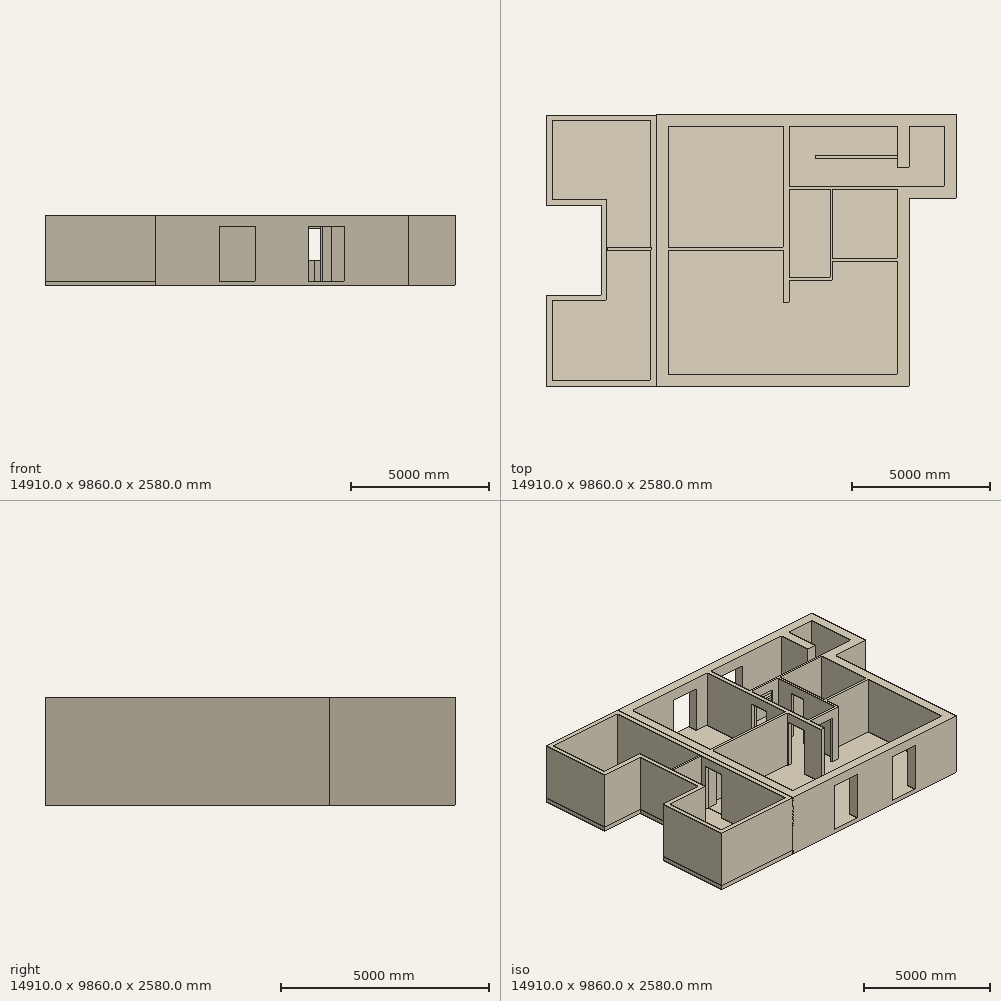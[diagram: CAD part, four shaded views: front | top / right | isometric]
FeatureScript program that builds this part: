
annotation { "Feature Type Name" : "Feature", "Feature Type Description" : "" }
export const myFeature = defineFeature(function(context is Context, id is Id, definition is map)
    precondition{}
    {
        {
            var Q0;
            Q0=qCreatedBy(makeId("Top.planeOp"),FACE);
            var sketch = newSketch(context, id + "F0", { "sketchPlane" : qUnion([Q0])});
            skLineSegment(sketch, "E0", {"start": v(0, 0) * mm, "end": v(0, 9860) * mm});
            skLineSegment(sketch, "E1", {"start": v(0, 9860) * mm, "end": v(10910, 9860) * mm});
            skLineSegment(sketch, "E2", {"start": v(10910, 9860) * mm, "end": v(10910, 6820) * mm});
            skLineSegment(sketch, "E3", {"start": v(10910, 6820) * mm, "end": v(9190, 6820) * mm});
            skLineSegment(sketch, "E4", {"start": v(9190, 6820) * mm, "end": v(9190, 0) * mm});
            skLineSegment(sketch, "E5", {"start": v(9190, 0) * mm, "end": v(0, 0) * mm});
            skLineSegment(sketch, "E6.0", {"start": v(8770, 7240) * mm, "end": v(8770, 420) * mm});
            skLineSegment(sketch, "E6.1", {"start": v(420, 420) * mm, "end": v(420, 4940) * mm});
            skLineSegment(sketch, "E6.2", {"start": v(420, 9440) * mm, "end": v(10490, 9440) * mm});
            skLineSegment(sketch, "E6.3", {"start": v(8770, 420) * mm, "end": v(420, 420) * mm});
            skLineSegment(sketch, "E6.4", {"start": v(10490, 9440) * mm, "end": v(10490, 7240) * mm});
            skLineSegment(sketch, "E6.5", {"start": v(10490, 7240) * mm, "end": v(8770, 7240) * mm});
            skLineSegment(sketch, "E7", {"start": v(420, 4940) * mm, "end": v(4620, 4940) * mm});
            skLineSegment(sketch, "E8.0", {"start": v(420, 5040) * mm, "end": v(4620, 5040) * mm});
            skLineSegment(sketch, "E9", {"start": v(4620, 5040) * mm, "end": v(4620, 4940) * mm});
            skLineSegment(sketch, "E10.trimOffspring", {"start": v(420, 5040) * mm, "end": v(420, 9440) * mm});
            skSolve(sketch);
        }
        {
            var Q0;
            Q0=makeQuery(id+"F0.imprint","IMPRINT",FACE,{"disambiguationData":[TD([[makeQuery(id+"F0.imprint","IMPRINT",EDGE,{"derivedFrom":sQuery(id+"F0.wireOp",EDGE,"E0")}),-1.0]])]});
            extrude(context, id + "F1", {"entities" : qUnion([Q0]), "depth" : 2400 * mm, "offsetDistance" : 25 * mm});
        }
        {
            var Q0;
            Q0=makeQuery(id+"F0.imprint","IMPRINT",FACE,{"disambiguationData":[TD([[makeQuery(id+"F0.imprint","IMPRINT",EDGE,{"derivedFrom":sQuery(id+"F0.wireOp",EDGE,"E0")}),-1.0]])]});
            var Q1;
            Q1=makeQuery(id+"F0.imprint","IMPRINT",FACE,{"disambiguationData":[TD([[makeQuery(id+"F0.imprint","IMPRINT",EDGE,{"derivedFrom":sQuery(id+"F0.wireOp",EDGE,"E6.0")}),-1.0]])]});
            extrude(context, id + "F2", {"entities" : qUnion([Q0, Q1]), "operationType" : NewBodyOperationType.ADD, "oppositeDirection" : true, "depth" : 180 * mm, "offsetDistance" : 25 * mm});
        }
        {
            var Q0;
            Q0=makeQuery(id+"F1.opExtrude","SWEPT_FACE",FACE,{"disambiguationData":[OSD([sQuery(id+"F0.wireOp",EDGE,"E6.3")])]});
            var sketch = newSketch(context, id + "F3", { "sketchPlane" : qUnion([Q0])});
            skLineSegment(sketch, "E11.bottom", {"start": v(-6870, 0) * mm, "end": v(-5570, 0) * mm});
            skLineSegment(sketch, "E11.top", {"start": v(-6870, 2000) * mm, "end": v(-5570, 2000) * mm});
            skLineSegment(sketch, "E11.left", {"start": v(-6870, 0) * mm, "end": v(-6870, 2000) * mm});
            skLineSegment(sketch, "E11.right", {"start": v(-5570, 0) * mm, "end": v(-5570, 2000) * mm});
            skLineSegment(sketch, "E12.bottom", {"start": v(-3620, 0) * mm, "end": v(-2320, 0) * mm});
            skLineSegment(sketch, "E12.top", {"start": v(-3620, 2000) * mm, "end": v(-2320, 2000) * mm});
            skLineSegment(sketch, "E12.left", {"start": v(-3620, 0) * mm, "end": v(-3620, 2000) * mm});
            skLineSegment(sketch, "E12.right", {"start": v(-2320, 0) * mm, "end": v(-2320, 2000) * mm});
            skSolve(sketch);
        }
        {
            var Q0;
            Q0=makeQuery(id+"F3.imprint","IMPRINT",FACE,{"disambiguationData":[TD([[makeQuery(id+"F3.imprint","IMPRINT",EDGE,{"derivedFrom":sQuery(id+"F3.wireOp",EDGE,"E11.bottom")}),1.0]])]});
            var Q1;
            Q1=makeQuery(id+"F3.imprint","IMPRINT",FACE,{"disambiguationData":[TD([[makeQuery(id+"F3.imprint","IMPRINT",EDGE,{"derivedFrom":sQuery(id+"F3.wireOp",EDGE,"E12.bottom")}),1.0]])]});
            extrude(context, id + "F4", {"entities" : qUnion([Q0, Q1]), "operationType" : NewBodyOperationType.REMOVE, "endBound" : BoundingType.UP_TO_NEXT, "oppositeDirection" : true, "depth" : 25 * mm, "offsetDistance" : 25 * mm});
        }
        {
            var Q0;
            Q0=makeQuery(id+"F4.boolean.opBoolean","MERGE",FACE,{"derivedFrom":[makeQuery(id+"F2.opExtrude","CAP_FACE",FACE,{"disambiguationData":[OSD([sQuery(id+"F0.wireOp",EDGE,"E0"),sQuery(id+"F0.wireOp",EDGE,"E1"),sQuery(id+"F0.wireOp",EDGE,"E2"),sQuery(id+"F0.wireOp",EDGE,"E3"),sQuery(id+"F0.wireOp",EDGE,"E4"),sQuery(id+"F0.wireOp",EDGE,"E5")])],"isStart":true}),makeQuery(id+"F4.opExtrude","SWEPT_FACE",FACE,{"disambiguationData":[OSD([sQuery(id+"F3.wireOp",EDGE,"E11.bottom")])]}),makeQuery(id+"F4.opExtrude","SWEPT_FACE",FACE,{"disambiguationData":[OSD([sQuery(id+"F3.wireOp",EDGE,"E12.bottom")])]})]});
            var sketch = newSketch(context, id + "F5", { "sketchPlane" : qUnion([Q0])});
            skLineSegment(sketch, "E13", {"start": v(4620, 9440) * mm, "end": v(4620, 3040) * mm});
            skLineSegment(sketch, "E14.0", {"start": v(4820, 9440) * mm, "end": v(4820, 3040) * mm});
            skLineSegment(sketch, "E15", {"start": v(4620, 3040) * mm, "end": v(4820, 3040) * mm});
            skSolve(sketch);
        }
        {
            var Q0;
            {var subQ0=sQuery(id+"F5.wireOp",EDGE,"E14.0");Q0=makeQuery(id+"F5.imprint","IMPRINT",FACE,{"disambiguationData":[TD([[makeQuery(id+"F5.imprint","IMPRINT",EDGE,{"derivedFrom":subQ0}),-1.0]])]});}
            extrude(context, id + "F6", {"entities" : qUnion([Q0]), "operationType" : NewBodyOperationType.ADD, "depth" : 2400 * mm, "offsetDistance" : 25 * mm});
        }
        {
            var Q0;
            {var subQ0=sQuery(id+"F0.wireOp",EDGE,"E5");Q0=makeQuery(id+"F6.boolean.opBoolean","SPLIT",FACE,{"disambiguationData":[TD([makeQuery(id+"F1.opExtrude","SWEPT_FACE",FACE,{"disambiguationData":[OSD([subQ0])]})])],"derivedFrom":makeQuery(id+"F4.boolean.opBoolean","MERGE",FACE,{"derivedFrom":[makeQuery(id+"F2.opExtrude","CAP_FACE",FACE,{"disambiguationData":[OSD([sQuery(id+"F0.wireOp",EDGE,"E0"),sQuery(id+"F0.wireOp",EDGE,"E1"),sQuery(id+"F0.wireOp",EDGE,"E2"),sQuery(id+"F0.wireOp",EDGE,"E3"),sQuery(id+"F0.wireOp",EDGE,"E4"),subQ0])],"isStart":true}),makeQuery(id+"F4.opExtrude","SWEPT_FACE",FACE,{"disambiguationData":[OSD([sQuery(id+"F3.wireOp",EDGE,"E11.bottom")])]}),makeQuery(id+"F4.opExtrude","SWEPT_FACE",FACE,{"disambiguationData":[OSD([sQuery(id+"F3.wireOp",EDGE,"E12.bottom")])]})]})});}
            var sketch = newSketch(context, id + "F7", { "sketchPlane" : qUnion([Q0])});
            skLineSegment(sketch, "E16", {"start": v(8770, 7240) * mm, "end": v(4820, 7240) * mm});
            skLineSegment(sketch, "E17.0", {"start": v(8770, 7140) * mm, "end": v(4820, 7140) * mm});
            skLineSegment(sketch, "E18.0", {"start": v(10490.26, 7239.74) * mm, "end": v(10490.26, 9440.26) * mm});
            skLineSegment(sketch, "E18.1", {"start": v(8770.26, 7239.74) * mm, "end": v(10490.26, 7239.74) * mm});
            skLineSegment(sketch, "E18.2", {"start": v(8770.26, 419.74) * mm, "end": v(8770.26, 7239.74) * mm});
            skLineSegment(sketch, "E18.3", {"start": v(6870.26, 419.74) * mm, "end": v(8770.26, 419.74) * mm});
            skLineSegment(sketch, "E18.4", {"start": v(6870.26, -0.26) * mm, "end": v(6870.26, 419.74) * mm});
            skLineSegment(sketch, "E18.5", {"start": v(10490.26, 9440.26) * mm, "end": v(4819.74, 9440.26) * mm});
            skLineSegment(sketch, "E18.6", {"start": v(5569.74, -0.26) * mm, "end": v(6870.26, -0.26) * mm});
            skLineSegment(sketch, "E18.7", {"start": v(5569.74, 419.74) * mm, "end": v(5569.74, -0.26) * mm});
            skLineSegment(sketch, "E18.8", {"start": v(4620.26, 4940.26) * mm, "end": v(419.74, 4940.26) * mm});
            skLineSegment(sketch, "E18.9", {"start": v(4620.26, 3040.26) * mm, "end": v(4620.26, 4940.26) * mm});
            skLineSegment(sketch, "E18.10", {"start": v(4819.74, 3040.26) * mm, "end": v(4620.26, 3040.26) * mm});
            skLineSegment(sketch, "E18.11", {"start": v(4819.74, 9440.26) * mm, "end": v(4819.74, 3040.26) * mm});
            skLineSegment(sketch, "E18.12", {"start": v(419.74, 4940.26) * mm, "end": v(419.74, 419.74) * mm});
            skLineSegment(sketch, "E18.13", {"start": v(419.74, 419.74) * mm, "end": v(2319.74, 419.74) * mm});
            skLineSegment(sketch, "E18.14", {"start": v(2319.74, 419.74) * mm, "end": v(2319.74, -0.26) * mm});
            skLineSegment(sketch, "E18.15", {"start": v(2319.74, -0.26) * mm, "end": v(3620.26, -0.26) * mm});
            skLineSegment(sketch, "E18.16", {"start": v(3620.26, -0.26) * mm, "end": v(3620.26, 419.74) * mm});
            skLineSegment(sketch, "E18.17", {"start": v(3620.26, 419.74) * mm, "end": v(5569.74, 419.74) * mm});
            skSolve(sketch);
        }
        {
            var Q0;
            {var subQ0=sQuery(id+"F7.wireOp",EDGE,"E18.2");var subQ1=sQuery(id+"F7.wireOp",EDGE,"E16");var subQ2=makeQuery(id+"F7.imprint","INTERSECT",VERTEX,{"derivedFrom":[subQ1,subQ0]});Q0=makeQuery(id+"F7.imprint","IMPRINT",FACE,{"disambiguationData":[TD([[makeQuery(id+"F7.imprint","IMPRINT",EDGE,{"disambiguationData":[TD([[subQ2,-1.0]])],"derivedFrom":subQ1}),1.0]])]});}
            extrude(context, id + "F8", {"entities" : qUnion([Q0]), "operationType" : NewBodyOperationType.ADD, "depth" : 2400 * mm, "offsetDistance" : 25 * mm});
        }
        {
            var Q0;
            {var subQ6=sQuery(id+"F0.wireOp",EDGE,"E5");var subQ7=makeQuery(id+"F1.opExtrude","SWEPT_FACE",FACE,{"disambiguationData":[OSD([subQ6])]});Q0=makeQuery(id+"F8.boolean.opBoolean","SPLIT",FACE,{"disambiguationData":[TD([subQ7])],"derivedFrom":makeQuery(id+"F6.boolean.opBoolean","SPLIT",FACE,{"disambiguationData":[TD([subQ7])],"derivedFrom":makeQuery(id+"F4.boolean.opBoolean","MERGE",FACE,{"derivedFrom":[makeQuery(id+"F2.opExtrude","CAP_FACE",FACE,{"disambiguationData":[OSD([sQuery(id+"F0.wireOp",EDGE,"E0"),sQuery(id+"F0.wireOp",EDGE,"E1"),sQuery(id+"F0.wireOp",EDGE,"E2"),sQuery(id+"F0.wireOp",EDGE,"E3"),sQuery(id+"F0.wireOp",EDGE,"E4"),subQ6])],"isStart":true}),makeQuery(id+"F4.opExtrude","SWEPT_FACE",FACE,{"disambiguationData":[OSD([sQuery(id+"F3.wireOp",EDGE,"E11.bottom")])]}),makeQuery(id+"F4.opExtrude","SWEPT_FACE",FACE,{"disambiguationData":[OSD([sQuery(id+"F3.wireOp",EDGE,"E12.bottom")])]})]})})});}
            var sketch = newSketch(context, id + "F9", { "sketchPlane" : qUnion([Q0])});
            skLineSegment(sketch, "E19", {"start": v(6315, 7140) * mm, "end": v(6315, 3840) * mm});
            skLineSegment(sketch, "E20.0", {"start": v(6415, 7140) * mm, "end": v(6415, 3840) * mm});
            skLineSegment(sketch, "E21", {"start": v(6415, 3840) * mm, "end": v(6315, 3840) * mm});
            skSolve(sketch);
        }
        {
            var Q0;
            {var subQ0=sQuery(id+"F9.wireOp",EDGE,"E19");Q0=makeQuery(id+"F9.imprint","IMPRINT",FACE,{"disambiguationData":[TD([[makeQuery(id+"F9.imprint","IMPRINT",EDGE,{"derivedFrom":subQ0}),1.0]])]});}
            extrude(context, id + "F10", {"entities" : qUnion([Q0]), "operationType" : NewBodyOperationType.ADD, "depth" : 2400 * mm, "offsetDistance" : 25 * mm});
        }
        {
            var Q0;
            {var subQ6=sQuery(id+"F0.wireOp",EDGE,"E5");var subQ7=makeQuery(id+"F1.opExtrude","SWEPT_FACE",FACE,{"disambiguationData":[OSD([subQ6])]});Q0=makeQuery(id+"F8.boolean.opBoolean","SPLIT",FACE,{"disambiguationData":[TD([subQ7])],"derivedFrom":makeQuery(id+"F6.boolean.opBoolean","SPLIT",FACE,{"disambiguationData":[TD([subQ7])],"derivedFrom":makeQuery(id+"F4.boolean.opBoolean","MERGE",FACE,{"derivedFrom":[makeQuery(id+"F2.opExtrude","CAP_FACE",FACE,{"disambiguationData":[OSD([sQuery(id+"F0.wireOp",EDGE,"E0"),sQuery(id+"F0.wireOp",EDGE,"E1"),sQuery(id+"F0.wireOp",EDGE,"E2"),sQuery(id+"F0.wireOp",EDGE,"E3"),sQuery(id+"F0.wireOp",EDGE,"E4"),subQ6])],"isStart":true}),makeQuery(id+"F4.opExtrude","SWEPT_FACE",FACE,{"disambiguationData":[OSD([sQuery(id+"F3.wireOp",EDGE,"E11.bottom")])]}),makeQuery(id+"F4.opExtrude","SWEPT_FACE",FACE,{"disambiguationData":[OSD([sQuery(id+"F3.wireOp",EDGE,"E12.bottom")])]})]})})});}
            var sketch = newSketch(context, id + "F11", { "sketchPlane" : qUnion([Q0])});
            skLineSegment(sketch, "E22", {"start": v(6415, 4640) * mm, "end": v(8770, 4640) * mm});
            skLineSegment(sketch, "E23.0", {"start": v(6415, 4540) * mm, "end": v(8770, 4540) * mm});
            skSolve(sketch);
        }
        {
            var Q0;
            {var subQ0=sQuery(id+"F11.wireOp",EDGE,"E22");Q0=makeQuery(id+"F11.imprint","IMPRINT",FACE,{"disambiguationData":[TD([[makeQuery(id+"F11.imprint","IMPRINT",EDGE,{"derivedFrom":subQ0}),-1.0]])]});}
            extrude(context, id + "F12", {"entities" : qUnion([Q0]), "operationType" : NewBodyOperationType.ADD, "depth" : 2400 * mm, "offsetDistance" : 25 * mm});
        }
        {
            var Q0;
            {var subQ6=sQuery(id+"F0.wireOp",EDGE,"E5");var subQ7=makeQuery(id+"F1.opExtrude","SWEPT_FACE",FACE,{"disambiguationData":[OSD([subQ6])]});Q0=makeQuery(id+"F12.boolean.opBoolean","SPLIT",FACE,{"disambiguationData":[TD([subQ7])],"derivedFrom":makeQuery(id+"F8.boolean.opBoolean","SPLIT",FACE,{"disambiguationData":[TD([subQ7])],"derivedFrom":makeQuery(id+"F6.boolean.opBoolean","SPLIT",FACE,{"disambiguationData":[TD([subQ7])],"derivedFrom":makeQuery(id+"F4.boolean.opBoolean","MERGE",FACE,{"derivedFrom":[makeQuery(id+"F2.opExtrude","CAP_FACE",FACE,{"disambiguationData":[OSD([sQuery(id+"F0.wireOp",EDGE,"E0"),sQuery(id+"F0.wireOp",EDGE,"E1"),sQuery(id+"F0.wireOp",EDGE,"E2"),sQuery(id+"F0.wireOp",EDGE,"E3"),sQuery(id+"F0.wireOp",EDGE,"E4"),subQ6])],"isStart":true}),makeQuery(id+"F4.opExtrude","SWEPT_FACE",FACE,{"disambiguationData":[OSD([sQuery(id+"F3.wireOp",EDGE,"E11.bottom")])]}),makeQuery(id+"F4.opExtrude","SWEPT_FACE",FACE,{"disambiguationData":[OSD([sQuery(id+"F3.wireOp",EDGE,"E12.bottom")])]})]})})})});}
            var sketch = newSketch(context, id + "F13", { "sketchPlane" : qUnion([Q0])});
            skLineSegment(sketch, "E24", {"start": v(6315, 3840) * mm, "end": v(4820, 3840) * mm});
            skLineSegment(sketch, "E25.0", {"start": v(6315, 3940) * mm, "end": v(4820, 3940) * mm});
            skLineSegment(sketch, "E26", {"start": v(4820, 3940) * mm, "end": v(4820, 3840) * mm});
            skLineSegment(sketch, "E27", {"start": v(6315, 3940) * mm, "end": v(6315, 3840) * mm});
            skSolve(sketch);
        }
        {
            var Q0;
            Q0=makeQuery(id+"F13.imprint","IMPRINT",FACE,{"disambiguationData":[TD([[makeQuery(id+"F13.imprint","IMPRINT",EDGE,{"derivedFrom":sQuery(id+"F13.wireOp",EDGE,"E24")}),-1.0]])]});
            extrude(context, id + "F14", {"entities" : qUnion([Q0]), "operationType" : NewBodyOperationType.ADD, "depth" : 2400 * mm, "offsetDistance" : 25 * mm});
        }
        {
            var Q0;
            Q0=makeQuery(id+"F14.boolean.opBoolean","MERGE",FACE,{"derivedFrom":[makeQuery(id+"F10.opExtrude","SWEPT_FACE",FACE,{"disambiguationData":[OSD([sQuery(id+"F9.wireOp",EDGE,"E21")])]}),makeQuery(id+"F14.opExtrude","SWEPT_FACE",FACE,{"disambiguationData":[OSD([sQuery(id+"F13.wireOp",EDGE,"E24")])]})]});
            var sketch = newSketch(context, id + "F15", { "sketchPlane" : qUnion([Q0])});
            skLineSegment(sketch, "E28.bottom", {"start": v(5140.9, 0) * mm, "end": v(6070.9, 0) * mm});
            skLineSegment(sketch, "E28.top", {"start": v(5140.9, 2000) * mm, "end": v(6070.9, 2000) * mm});
            skLineSegment(sketch, "E28.left", {"start": v(5140.9, 0) * mm, "end": v(5140.9, 2000) * mm});
            skLineSegment(sketch, "E28.right", {"start": v(6070.9, 0) * mm, "end": v(6070.9, 2000) * mm});
            skSolve(sketch);
        }
        {
            var Q0;
            Q0=makeQuery(id+"F15.imprint","IMPRINT",FACE,{"disambiguationData":[TD([[makeQuery(id+"F15.imprint","IMPRINT",EDGE,{"derivedFrom":sQuery(id+"F15.wireOp",EDGE,"E28.bottom")}),-1.0]])]});
            extrude(context, id + "F16", {"entities" : qUnion([Q0]), "operationType" : NewBodyOperationType.REMOVE, "oppositeDirection" : true, "depth" : 870 * mm, "offsetDistance" : 25 * mm});
        }
        {
            var Q0;
            {var subQ1=sQuery(id+"F7.wireOp",EDGE,"E17.0");var subQ2=makeQuery(id+"F8.opExtrude","SWEPT_FACE",FACE,{"disambiguationData":[OSD([subQ1])]});var subQ3=sQuery(id+"F5.wireOp",EDGE,"E14.0");var subQ15=sQuery(id+"F5.wireOp",EDGE,"E15");Q0=makeQuery(id+"F14.boolean.opBoolean","SPLIT",FACE,{"disambiguationData":[TD([subQ2])],"derivedFrom":makeQuery(id+"F8.boolean.opBoolean","SPLIT",FACE,{"disambiguationData":[TD([makeQuery(id+"F6.opExtrude","SWEPT_FACE",FACE,{"disambiguationData":[OSD([subQ15])]})])],"derivedFrom":makeQuery(id+"F6.opExtrude","SWEPT_FACE",FACE,{"disambiguationData":[OSD([subQ3])]})})});}
            var sketch = newSketch(context, id + "F17", { "sketchPlane" : qUnion([Q0])});
            skLineSegment(sketch, "E29.bottom", {"start": v(3992.78, 0) * mm, "end": v(4892.78, 0) * mm});
            skLineSegment(sketch, "E29.top", {"start": v(3992.78, 2000) * mm, "end": v(4892.78, 2000) * mm});
            skLineSegment(sketch, "E29.left", {"start": v(3992.78, 0) * mm, "end": v(3992.78, 2000) * mm});
            skLineSegment(sketch, "E29.right", {"start": v(4892.78, 0) * mm, "end": v(4892.78, 2000) * mm});
            skSolve(sketch);
        }
        {
            var Q0;
            Q0=makeQuery(id+"F17.imprint","IMPRINT",FACE,{"disambiguationData":[TD([[makeQuery(id+"F17.imprint","IMPRINT",EDGE,{"derivedFrom":sQuery(id+"F17.wireOp",EDGE,"E29.bottom")}),-1.0]])]});
            extrude(context, id + "F18", {"entities" : qUnion([Q0]), "operationType" : NewBodyOperationType.REMOVE, "oppositeDirection" : true, "depth" : 770 * mm, "offsetDistance" : 25 * mm});
        }
        {
            var Q0;
            {var subQ1=sQuery(id+"F9.wireOp",EDGE,"E20.0");var subQ11=sQuery(id+"F7.wireOp",EDGE,"E17.0");Q0=makeQuery(id+"F12.boolean.opBoolean","SPLIT",FACE,{"disambiguationData":[TD([makeQuery(id+"F8.opExtrude","SWEPT_FACE",FACE,{"disambiguationData":[OSD([subQ11])]})])],"derivedFrom":makeQuery(id+"F10.opExtrude","SWEPT_FACE",FACE,{"disambiguationData":[OSD([subQ1])]})});}
            var sketch = newSketch(context, id + "F19", { "sketchPlane" : qUnion([Q0])});
            skLineSegment(sketch, "E30.bottom", {"start": v(6410, 0) * mm, "end": v(5710, 0) * mm});
            skLineSegment(sketch, "E30.top", {"start": v(6410, 2000) * mm, "end": v(5710, 2000) * mm});
            skLineSegment(sketch, "E30.left", {"start": v(6410, 0) * mm, "end": v(6410, 2000) * mm});
            skLineSegment(sketch, "E30.right", {"start": v(5710, 0) * mm, "end": v(5710, 2000) * mm});
            skSolve(sketch);
        }
        {
            var Q0;
            Q0=makeQuery(id+"F19.imprint","IMPRINT",FACE,{"disambiguationData":[TD([[makeQuery(id+"F19.imprint","IMPRINT",EDGE,{"derivedFrom":sQuery(id+"F19.wireOp",EDGE,"E30.bottom")}),-1.0]])]});
            extrude(context, id + "F20", {"entities" : qUnion([Q0]), "operationType" : NewBodyOperationType.REMOVE, "oppositeDirection" : true, "depth" : 580 * mm, "offsetDistance" : 25 * mm});
        }
        {
            var Q0;
            {var subQ1=sQuery(id+"F0.wireOp",EDGE,"E6.2");var subQ8=sQuery(id+"F5.wireOp",EDGE,"E13");Q0=makeQuery(id+"F6.boolean.opBoolean","SPLIT",FACE,{"disambiguationData":[TD([makeQuery(id+"F1.opExtrude","SWEPT_FACE",FACE,{"disambiguationData":[OSD([subQ1])]})])],"derivedFrom":makeQuery(id+"F6.opExtrude","SWEPT_FACE",FACE,{"disambiguationData":[OSD([subQ8])]})});}
            var sketch = newSketch(context, id + "F21", { "sketchPlane" : qUnion([Q0])});
            skLineSegment(sketch, "E31.bottom", {"start": v(-6970, 0) * mm, "end": v(-6100, 0) * mm});
            skLineSegment(sketch, "E31.top", {"start": v(-6970, 2000) * mm, "end": v(-6100, 2000) * mm});
            skLineSegment(sketch, "E31.left", {"start": v(-6970, 0) * mm, "end": v(-6970, 2000) * mm});
            skLineSegment(sketch, "E31.right", {"start": v(-6100, 0) * mm, "end": v(-6100, 2000) * mm});
            skSolve(sketch);
        }
        {
            var Q0;
            Q0=makeQuery(id+"F21.imprint","IMPRINT",FACE,{"disambiguationData":[TD([[makeQuery(id+"F21.imprint","IMPRINT",EDGE,{"derivedFrom":sQuery(id+"F21.wireOp",EDGE,"E31.bottom")}),1.0]])]});
            extrude(context, id + "F22", {"entities" : qUnion([Q0]), "operationType" : NewBodyOperationType.REMOVE, "oppositeDirection" : true, "depth" : 1270 * mm, "offsetDistance" : 25 * mm});
        }
        {
            var Q0;
            {var subQ6=sQuery(id+"F5.wireOp",EDGE,"E14.0");var subQ10=sQuery(id+"F7.wireOp",EDGE,"E17.0");Q0=makeQuery(id+"F10.boolean.opBoolean","SPLIT",FACE,{"disambiguationData":[TD([makeQuery(id+"F6.opExtrude","SWEPT_FACE",FACE,{"disambiguationData":[OSD([subQ6])]})])],"derivedFrom":makeQuery(id+"F8.opExtrude","SWEPT_FACE",FACE,{"disambiguationData":[OSD([subQ10])]})});}
            var sketch = newSketch(context, id + "F23", { "sketchPlane" : qUnion([Q0])});
            skLineSegment(sketch, "E32.bottom", {"start": v(5095, 0) * mm, "end": v(6015, 0) * mm});
            skLineSegment(sketch, "E32.top", {"start": v(5095, 2000) * mm, "end": v(6015, 2000) * mm});
            skLineSegment(sketch, "E32.left", {"start": v(5095, 0) * mm, "end": v(5095, 2000) * mm});
            skLineSegment(sketch, "E32.right", {"start": v(6015, 0) * mm, "end": v(6015, 2000) * mm});
            skSolve(sketch);
        }
        {
            var Q0;
            Q0=makeQuery(id+"F23.imprint","IMPRINT",FACE,{"disambiguationData":[TD([[makeQuery(id+"F23.imprint","IMPRINT",EDGE,{"derivedFrom":sQuery(id+"F23.wireOp",EDGE,"E32.bottom")}),-1.0]])]});
            extrude(context, id + "F24", {"entities" : qUnion([Q0]), "operationType" : NewBodyOperationType.REMOVE, "oppositeDirection" : true, "depth" : 640 * mm, "offsetDistance" : 25 * mm});
        }
        {
            var Q0;
            {var subQ2=makeQuery(id+"F8.opExtrude","SWEPT_FACE",FACE,{"disambiguationData":[OSD([sQuery(id+"F7.wireOp",EDGE,"E17.0")])]});var subQ9=sQuery(id+"F0.wireOp",EDGE,"E5");var subQ10=makeQuery(id+"F1.opExtrude","SWEPT_FACE",FACE,{"disambiguationData":[OSD([subQ9])]});var subQ19=makeQuery(id+"F1.opExtrude","SWEPT_FACE",FACE,{"disambiguationData":[OSD([sQuery(id+"F0.wireOp",EDGE,"E6.2")])]});var subQ22=makeQuery(id+"F4.boolean.opBoolean","MERGE",FACE,{"derivedFrom":[makeQuery(id+"F2.opExtrude","CAP_FACE",FACE,{"disambiguationData":[OSD([sQuery(id+"F0.wireOp",EDGE,"E0"),sQuery(id+"F0.wireOp",EDGE,"E1"),sQuery(id+"F0.wireOp",EDGE,"E2"),sQuery(id+"F0.wireOp",EDGE,"E3"),sQuery(id+"F0.wireOp",EDGE,"E4"),subQ9])],"isStart":true}),makeQuery(id+"F4.opExtrude","SWEPT_FACE",FACE,{"disambiguationData":[OSD([sQuery(id+"F3.wireOp",EDGE,"E11.bottom")])]}),makeQuery(id+"F4.opExtrude","SWEPT_FACE",FACE,{"disambiguationData":[OSD([sQuery(id+"F3.wireOp",EDGE,"E12.bottom")])]})]});var subQ23=makeQuery(id+"F6.boolean.opBoolean","SPLIT",FACE,{"disambiguationData":[TD([subQ10])],"derivedFrom":subQ22});var subQ24=makeQuery(id+"F8.boolean.opBoolean","SPLIT",FACE,{"disambiguationData":[TD([subQ10])],"derivedFrom":subQ23});var subQ25=makeQuery(id+"F12.boolean.opBoolean","SPLIT",FACE,{"disambiguationData":[TD([subQ10])],"derivedFrom":subQ24});Q0=makeQuery(id+"F24.boolean.opBoolean","MERGE",FACE,{"derivedFrom":[makeQuery(id+"F8.boolean.opBoolean","SPLIT",FACE,{"disambiguationData":[TD([subQ19])],"derivedFrom":subQ23}),makeQuery(id+"F22.boolean.opBoolean","MERGE",FACE,{"derivedFrom":[makeQuery(id+"F6.boolean.opBoolean","SPLIT",FACE,{"disambiguationData":[TD([makeQuery(id+"F1.opExtrude","SWEPT_FACE",FACE,{"disambiguationData":[OSD([sQuery(id+"F0.wireOp",EDGE,"E8.0")])]})])],"derivedFrom":subQ22}),makeQuery(id+"F20.boolean.opBoolean","MERGE",FACE,{"derivedFrom":[makeQuery(id+"F12.boolean.opBoolean","SPLIT",FACE,{"disambiguationData":[TD([makeQuery(id+"F12.opExtrude","SWEPT_FACE",FACE,{"disambiguationData":[OSD([sQuery(id+"F11.wireOp",EDGE,"E22")])]})])],"derivedFrom":subQ24}),makeQuery(id+"F18.boolean.opBoolean","MERGE",FACE,{"derivedFrom":[makeQuery(id+"F16.boolean.opBoolean","MERGE",FACE,{"derivedFrom":[makeQuery(id+"F14.boolean.opBoolean","SPLIT",FACE,{"disambiguationData":[TD([subQ10])],"derivedFrom":subQ25}),makeQuery(id+"F14.boolean.opBoolean","SPLIT",FACE,{"disambiguationData":[TD([subQ2])],"derivedFrom":subQ25}),makeQuery(id+"F16.opExtrude","SWEPT_FACE",FACE,{"disambiguationData":[OSD([sQuery(id+"F15.wireOp",EDGE,"E28.bottom")])]})]}),makeQuery(id+"F18.opExtrude","SWEPT_FACE",FACE,{"disambiguationData":[OSD([sQuery(id+"F17.wireOp",EDGE,"E29.bottom")])]})]}),makeQuery(id+"F20.opExtrude","SWEPT_FACE",FACE,{"disambiguationData":[OSD([sQuery(id+"F19.wireOp",EDGE,"E30.bottom")])]})]}),makeQuery(id+"F22.opExtrude","SWEPT_FACE",FACE,{"disambiguationData":[OSD([sQuery(id+"F21.wireOp",EDGE,"E31.bottom")])]})]}),makeQuery(id+"F24.opExtrude","SWEPT_FACE",FACE,{"disambiguationData":[OSD([sQuery(id+"F23.wireOp",EDGE,"E32.bottom")])]})]});}
            var sketch = newSketch(context, id + "F25", { "sketchPlane" : qUnion([Q0])});
            skLineSegment(sketch, "E33", {"start": v(8770, 9440) * mm, "end": v(8770, 7940) * mm});
            skLineSegment(sketch, "E34.0", {"start": v(9190, 9440) * mm, "end": v(9190, 7940) * mm});
            skLineSegment(sketch, "E35", {"start": v(8770, 7940) * mm, "end": v(9190, 7940) * mm});
            skSolve(sketch);
        }
        {
            var Q0;
            {var subQ0=sQuery(id+"F25.wireOp",EDGE,"E33");Q0=makeQuery(id+"F25.imprint","IMPRINT",FACE,{"disambiguationData":[TD([[makeQuery(id+"F25.imprint","IMPRINT",EDGE,{"derivedFrom":subQ0}),1.0]])]});}
            extrude(context, id + "F26", {"entities" : qUnion([Q0]), "operationType" : NewBodyOperationType.ADD, "depth" : 2400 * mm, "offsetDistance" : 25 * mm});
        }
        {
            var Q0;
            {var subQ2=makeQuery(id+"F8.opExtrude","SWEPT_FACE",FACE,{"disambiguationData":[OSD([sQuery(id+"F7.wireOp",EDGE,"E17.0")])]});var subQ9=sQuery(id+"F0.wireOp",EDGE,"E5");var subQ10=makeQuery(id+"F1.opExtrude","SWEPT_FACE",FACE,{"disambiguationData":[OSD([subQ9])]});var subQ19=makeQuery(id+"F1.opExtrude","SWEPT_FACE",FACE,{"disambiguationData":[OSD([sQuery(id+"F0.wireOp",EDGE,"E6.2")])]});var subQ22=makeQuery(id+"F4.boolean.opBoolean","MERGE",FACE,{"derivedFrom":[makeQuery(id+"F2.opExtrude","CAP_FACE",FACE,{"disambiguationData":[OSD([sQuery(id+"F0.wireOp",EDGE,"E0"),sQuery(id+"F0.wireOp",EDGE,"E1"),sQuery(id+"F0.wireOp",EDGE,"E2"),sQuery(id+"F0.wireOp",EDGE,"E3"),sQuery(id+"F0.wireOp",EDGE,"E4"),subQ9])],"isStart":true}),makeQuery(id+"F4.opExtrude","SWEPT_FACE",FACE,{"disambiguationData":[OSD([sQuery(id+"F3.wireOp",EDGE,"E11.bottom")])]}),makeQuery(id+"F4.opExtrude","SWEPT_FACE",FACE,{"disambiguationData":[OSD([sQuery(id+"F3.wireOp",EDGE,"E12.bottom")])]})]});var subQ23=makeQuery(id+"F6.boolean.opBoolean","SPLIT",FACE,{"disambiguationData":[TD([subQ10])],"derivedFrom":subQ22});var subQ24=makeQuery(id+"F8.boolean.opBoolean","SPLIT",FACE,{"disambiguationData":[TD([subQ10])],"derivedFrom":subQ23});var subQ25=makeQuery(id+"F12.boolean.opBoolean","SPLIT",FACE,{"disambiguationData":[TD([subQ10])],"derivedFrom":subQ24});Q0=makeQuery(id+"F24.boolean.opBoolean","MERGE",FACE,{"derivedFrom":[makeQuery(id+"F8.boolean.opBoolean","SPLIT",FACE,{"disambiguationData":[TD([subQ19])],"derivedFrom":subQ23}),makeQuery(id+"F22.boolean.opBoolean","MERGE",FACE,{"derivedFrom":[makeQuery(id+"F6.boolean.opBoolean","SPLIT",FACE,{"disambiguationData":[TD([makeQuery(id+"F1.opExtrude","SWEPT_FACE",FACE,{"disambiguationData":[OSD([sQuery(id+"F0.wireOp",EDGE,"E8.0")])]})])],"derivedFrom":subQ22}),makeQuery(id+"F20.boolean.opBoolean","MERGE",FACE,{"derivedFrom":[makeQuery(id+"F12.boolean.opBoolean","SPLIT",FACE,{"disambiguationData":[TD([makeQuery(id+"F12.opExtrude","SWEPT_FACE",FACE,{"disambiguationData":[OSD([sQuery(id+"F11.wireOp",EDGE,"E22")])]})])],"derivedFrom":subQ24}),makeQuery(id+"F18.boolean.opBoolean","MERGE",FACE,{"derivedFrom":[makeQuery(id+"F16.boolean.opBoolean","MERGE",FACE,{"derivedFrom":[makeQuery(id+"F14.boolean.opBoolean","SPLIT",FACE,{"disambiguationData":[TD([subQ10])],"derivedFrom":subQ25}),makeQuery(id+"F14.boolean.opBoolean","SPLIT",FACE,{"disambiguationData":[TD([subQ2])],"derivedFrom":subQ25}),makeQuery(id+"F16.opExtrude","SWEPT_FACE",FACE,{"disambiguationData":[OSD([sQuery(id+"F15.wireOp",EDGE,"E28.bottom")])]})]}),makeQuery(id+"F18.opExtrude","SWEPT_FACE",FACE,{"disambiguationData":[OSD([sQuery(id+"F17.wireOp",EDGE,"E29.bottom")])]})]}),makeQuery(id+"F20.opExtrude","SWEPT_FACE",FACE,{"disambiguationData":[OSD([sQuery(id+"F19.wireOp",EDGE,"E30.bottom")])]})]}),makeQuery(id+"F22.opExtrude","SWEPT_FACE",FACE,{"disambiguationData":[OSD([sQuery(id+"F21.wireOp",EDGE,"E31.bottom")])]})]}),makeQuery(id+"F24.opExtrude","SWEPT_FACE",FACE,{"disambiguationData":[OSD([sQuery(id+"F23.wireOp",EDGE,"E32.bottom")])]})]});}
            var sketch = newSketch(context, id + "F27", { "sketchPlane" : qUnion([Q0])});
            skLineSegment(sketch, "E36", {"start": v(8770, 8390) * mm, "end": v(5770, 8390) * mm});
            skLineSegment(sketch, "E37.0", {"start": v(8770, 8270) * mm, "end": v(5770, 8270) * mm});
            skLineSegment(sketch, "E38", {"start": v(5770, 8390) * mm, "end": v(5770, 8270) * mm});
            skSolve(sketch);
        }
        {
            var Q0;
            {var subQ0=sQuery(id+"F27.wireOp",EDGE,"E36");Q0=makeQuery(id+"F27.imprint","IMPRINT",FACE,{"disambiguationData":[TD([[makeQuery(id+"F27.imprint","IMPRINT",EDGE,{"derivedFrom":subQ0}),1.0]])]});}
            extrude(context, id + "F28", {"entities" : qUnion([Q0]), "operationType" : NewBodyOperationType.ADD, "depth" : 750 * mm, "offsetDistance" : 25 * mm});
        }
        {
            var Q0;
            {var subQ7=sQuery(id+"F0.wireOp",EDGE,"E6.2");var subQ8=sQuery(id+"F0.wireOp",EDGE,"E10.trimOffspring");Q0=makeQuery(id+"F6.boolean.opBoolean","SPLIT",FACE,{"disambiguationData":[TD([makeQuery(id+"F1.opExtrude","SWEPT_FACE",FACE,{"disambiguationData":[OSD([subQ8])]})])],"derivedFrom":makeQuery(id+"F1.opExtrude","SWEPT_FACE",FACE,{"disambiguationData":[OSD([subQ7])]})});}
            var sketch = newSketch(context, id + "F29", { "sketchPlane" : qUnion([Q0])});
            skLineSegment(sketch, "E39.bottom", {"start": v(2720, 0) * mm, "end": v(4020, 0) * mm});
            skLineSegment(sketch, "E39.top", {"start": v(2720, 1900) * mm, "end": v(4020, 1900) * mm});
            skLineSegment(sketch, "E39.left", {"start": v(2720, 0) * mm, "end": v(2720, 1900) * mm});
            skLineSegment(sketch, "E39.right", {"start": v(4020, 0) * mm, "end": v(4020, 1900) * mm});
            skSolve(sketch);
        }
        {
            var Q0;
            Q0=makeQuery(id+"F29.imprint","IMPRINT",FACE,{"disambiguationData":[TD([[makeQuery(id+"F29.imprint","IMPRINT",EDGE,{"derivedFrom":sQuery(id+"F29.wireOp",EDGE,"E39.bottom")}),1.0]])]});
            extrude(context, id + "F30", {"entities" : qUnion([Q0]), "operationType" : NewBodyOperationType.REMOVE, "oppositeDirection" : true, "depth" : 2380 * mm, "offsetDistance" : 25 * mm});
        }
        {
            var Q0;
            {var subQ2=sQuery(id+"F5.wireOp",EDGE,"E14.0");var subQ6=makeQuery(id+"F6.opExtrude","SWEPT_FACE",FACE,{"disambiguationData":[OSD([subQ2])]});var subQ7=sQuery(id+"F0.wireOp",EDGE,"E6.4");var subQ8=sQuery(id+"F0.wireOp",EDGE,"E6.2");Q0=makeQuery(id+"F26.boolean.opBoolean","SPLIT",FACE,{"disambiguationData":[TD([subQ6])],"derivedFrom":makeQuery(id+"F6.boolean.opBoolean","SPLIT",FACE,{"disambiguationData":[TD([makeQuery(id+"F1.opExtrude","SWEPT_FACE",FACE,{"disambiguationData":[OSD([subQ7])]})])],"derivedFrom":makeQuery(id+"F1.opExtrude","SWEPT_FACE",FACE,{"disambiguationData":[OSD([subQ8])]})})});}
            var sketch = newSketch(context, id + "F31", { "sketchPlane" : qUnion([Q0])});
            skLineSegment(sketch, "E40.bottom", {"start": v(5370, 1900) * mm, "end": v(6620, 1900) * mm});
            skLineSegment(sketch, "E40.top", {"start": v(5370, 750) * mm, "end": v(6620, 750) * mm});
            skLineSegment(sketch, "E40.left", {"start": v(5370, 1900) * mm, "end": v(5370, 750) * mm});
            skLineSegment(sketch, "E40.right", {"start": v(6620, 1900) * mm, "end": v(6620, 750) * mm});
            skSolve(sketch);
        }
        {
            var Q0;
            Q0=makeQuery(id+"F31.imprint","IMPRINT",FACE,{"disambiguationData":[TD([[makeQuery(id+"F31.imprint","IMPRINT",EDGE,{"derivedFrom":sQuery(id+"F31.wireOp",EDGE,"E40.bottom")}),-1.0]])]});
            extrude(context, id + "F32", {"entities" : qUnion([Q0]), "operationType" : NewBodyOperationType.REMOVE, "oppositeDirection" : true, "depth" : 1650 * mm, "offsetDistance" : 25 * mm});
        }
        {
            var Q0;
            Q0=makeQuery(id+"F1.opExtrude","SWEPT_FACE",FACE,{"disambiguationData":[OSD([sQuery(id+"F0.wireOp",EDGE,"E6.1")])]});
            var sketch = newSketch(context, id + "F33", { "sketchPlane" : qUnion([Q0])});
            skLineSegment(sketch, "E41.bottom", {"start": v(3840, 0) * mm, "end": v(4740, 0) * mm});
            skLineSegment(sketch, "E41.top", {"start": v(3840, 2000) * mm, "end": v(4740, 2000) * mm});
            skLineSegment(sketch, "E41.left", {"start": v(3840, 0) * mm, "end": v(3840, 2000) * mm});
            skLineSegment(sketch, "E41.right", {"start": v(4740, 0) * mm, "end": v(4740, 2000) * mm});
            skSolve(sketch);
        }
        {
            var Q0;
            Q0=makeQuery(id+"F33.imprint","IMPRINT",FACE,{"disambiguationData":[TD([[makeQuery(id+"F33.imprint","IMPRINT",EDGE,{"derivedFrom":sQuery(id+"F33.wireOp",EDGE,"E41.bottom")}),1.0]])]});
            extrude(context, id + "F34", {"entities" : qUnion([Q0]), "operationType" : NewBodyOperationType.REMOVE, "oppositeDirection" : true, "depth" : 1250 * mm, "offsetDistance" : 25 * mm});
        }
        {
            var Q0;
            {var subQ2=makeQuery(id+"F8.opExtrude","SWEPT_FACE",FACE,{"disambiguationData":[OSD([sQuery(id+"F7.wireOp",EDGE,"E17.0")])]});var subQ9=sQuery(id+"F0.wireOp",EDGE,"E5");var subQ10=makeQuery(id+"F1.opExtrude","SWEPT_FACE",FACE,{"disambiguationData":[OSD([subQ9])]});var subQ19=makeQuery(id+"F1.opExtrude","SWEPT_FACE",FACE,{"disambiguationData":[OSD([sQuery(id+"F0.wireOp",EDGE,"E6.2")])]});var subQ22=makeQuery(id+"F4.boolean.opBoolean","MERGE",FACE,{"derivedFrom":[makeQuery(id+"F2.opExtrude","CAP_FACE",FACE,{"disambiguationData":[OSD([sQuery(id+"F0.wireOp",EDGE,"E0"),sQuery(id+"F0.wireOp",EDGE,"E1"),sQuery(id+"F0.wireOp",EDGE,"E2"),sQuery(id+"F0.wireOp",EDGE,"E3"),sQuery(id+"F0.wireOp",EDGE,"E4"),subQ9])],"isStart":true}),makeQuery(id+"F4.opExtrude","SWEPT_FACE",FACE,{"disambiguationData":[OSD([sQuery(id+"F3.wireOp",EDGE,"E11.bottom")])]}),makeQuery(id+"F4.opExtrude","SWEPT_FACE",FACE,{"disambiguationData":[OSD([sQuery(id+"F3.wireOp",EDGE,"E12.bottom")])]})]});var subQ23=makeQuery(id+"F6.boolean.opBoolean","SPLIT",FACE,{"disambiguationData":[TD([subQ10])],"derivedFrom":subQ22});var subQ24=makeQuery(id+"F8.boolean.opBoolean","SPLIT",FACE,{"disambiguationData":[TD([subQ10])],"derivedFrom":subQ23});var subQ25=makeQuery(id+"F12.boolean.opBoolean","SPLIT",FACE,{"disambiguationData":[TD([subQ10])],"derivedFrom":subQ24});Q0=makeQuery(id+"F34.boolean.opBoolean","MERGE",FACE,{"derivedFrom":[makeQuery(id+"F30.boolean.opBoolean","MERGE",FACE,{"derivedFrom":[makeQuery(id+"F24.boolean.opBoolean","MERGE",FACE,{"derivedFrom":[makeQuery(id+"F8.boolean.opBoolean","SPLIT",FACE,{"disambiguationData":[TD([subQ19])],"derivedFrom":subQ23}),makeQuery(id+"F22.boolean.opBoolean","MERGE",FACE,{"derivedFrom":[makeQuery(id+"F6.boolean.opBoolean","SPLIT",FACE,{"disambiguationData":[TD([makeQuery(id+"F1.opExtrude","SWEPT_FACE",FACE,{"disambiguationData":[OSD([sQuery(id+"F0.wireOp",EDGE,"E8.0")])]})])],"derivedFrom":subQ22}),makeQuery(id+"F20.boolean.opBoolean","MERGE",FACE,{"derivedFrom":[makeQuery(id+"F12.boolean.opBoolean","SPLIT",FACE,{"disambiguationData":[TD([makeQuery(id+"F12.opExtrude","SWEPT_FACE",FACE,{"disambiguationData":[OSD([sQuery(id+"F11.wireOp",EDGE,"E22")])]})])],"derivedFrom":subQ24}),makeQuery(id+"F18.boolean.opBoolean","MERGE",FACE,{"derivedFrom":[makeQuery(id+"F16.boolean.opBoolean","MERGE",FACE,{"derivedFrom":[makeQuery(id+"F14.boolean.opBoolean","SPLIT",FACE,{"disambiguationData":[TD([subQ10])],"derivedFrom":subQ25}),makeQuery(id+"F14.boolean.opBoolean","SPLIT",FACE,{"disambiguationData":[TD([subQ2])],"derivedFrom":subQ25}),makeQuery(id+"F16.opExtrude","SWEPT_FACE",FACE,{"disambiguationData":[OSD([sQuery(id+"F15.wireOp",EDGE,"E28.bottom")])]})]}),makeQuery(id+"F18.opExtrude","SWEPT_FACE",FACE,{"disambiguationData":[OSD([sQuery(id+"F17.wireOp",EDGE,"E29.bottom")])]})]}),makeQuery(id+"F20.opExtrude","SWEPT_FACE",FACE,{"disambiguationData":[OSD([sQuery(id+"F19.wireOp",EDGE,"E30.bottom")])]})]}),makeQuery(id+"F22.opExtrude","SWEPT_FACE",FACE,{"disambiguationData":[OSD([sQuery(id+"F21.wireOp",EDGE,"E31.bottom")])]})]}),makeQuery(id+"F24.opExtrude","SWEPT_FACE",FACE,{"disambiguationData":[OSD([sQuery(id+"F23.wireOp",EDGE,"E32.bottom")])]})]}),makeQuery(id+"F30.opExtrude","SWEPT_FACE",FACE,{"disambiguationData":[OSD([sQuery(id+"F29.wireOp",EDGE,"E39.bottom")])]})]}),makeQuery(id+"F34.opExtrude","SWEPT_FACE",FACE,{"disambiguationData":[OSD([sQuery(id+"F33.wireOp",EDGE,"E41.bottom")])]})]});}
            var sketch = newSketch(context, id + "F35", { "sketchPlane" : qUnion([Q0])});
            skLineSegment(sketch, "E42", {"start": v(0, 9854.27) * mm, "end": v(-4000, 9854.27) * mm});
            skLineSegment(sketch, "E43", {"start": v(-4000, 9854.27) * mm, "end": v(-4000, 6574.27) * mm});
            skLineSegment(sketch, "E44", {"start": v(-4000, 6574.27) * mm, "end": v(-2000, 6574.27) * mm});
            skLineSegment(sketch, "E45", {"start": v(-2000, 6574.27) * mm, "end": v(-2000, 3294.27) * mm});
            skLineSegment(sketch, "E46", {"start": v(-2000, 3294.27) * mm, "end": v(-4000, 3294.27) * mm});
            skLineSegment(sketch, "E47", {"start": v(-4000, 3294.27) * mm, "end": v(-4000, 0) * mm});
            skLineSegment(sketch, "E48", {"start": v(-4000, 0) * mm, "end": v(0, 0) * mm});
            skLineSegment(sketch, "E49", {"start": v(0, 9854.27) * mm, "end": v(0, 0) * mm});
            skSolve(sketch);
        }
        {
            var Q0;
            {var subQ1=sQuery(id+"F35.wireOp",EDGE,"efdb84b2-dbaf-4d21-8679-9f55b8f338ee.1");Q0=makeQuery(id+"F35.imprint","IMPRINT",FACE,{"disambiguationData":[TD([[makeQuery(id+"F35.imprint","IMPRINT",EDGE,{"derivedFrom":subQ1}),1.0]])]});}
            var Q1;
            {var subQ7=sQuery(id+"F35.wireOp",EDGE,"E42");Q1=makeQuery(id+"F35.imprint","IMPRINT",FACE,{"disambiguationData":[TD([[makeQuery(id+"F35.imprint","IMPRINT",EDGE,{"derivedFrom":subQ7}),1.0]])]});}
            extrude(context, id + "F36", {"entities" : qUnion([Q0, Q1]), "oppositeDirection" : true, "depth" : 180 * mm, "offsetDistance" : 25 * mm, "hasSecondDirection" : true, "secondDirectionOppositeDirection" : false, "secondDirectionDepth" : 0 * mm});
        }
        {
            var Q0;
            Q0=makeQuery(id+"F36.opExtrude","CAP_FACE",FACE,{"disambiguationData":[OSD([sQuery(id+"F35.wireOp",EDGE,"E42"),sQuery(id+"F35.wireOp",EDGE,"E43"),sQuery(id+"F35.wireOp",EDGE,"E44"),sQuery(id+"F35.wireOp",EDGE,"E45"),sQuery(id+"F35.wireOp",EDGE,"E46"),sQuery(id+"F35.wireOp",EDGE,"E47"),sQuery(id+"F35.wireOp",EDGE,"E48"),sQuery(id+"F35.wireOp",EDGE,"E49")])],"isStart":true});
            var sketch = newSketch(context, id + "F37", { "sketchPlane" : qUnion([Q0])});
            skLineSegment(sketch, "E50", {"start": v(0, 9854.27) * mm, "end": v(-4000, 9854.27) * mm});
            skLineSegment(sketch, "E51", {"start": v(-4000, 9854.27) * mm, "end": v(-4000, 6574.27) * mm});
            skLineSegment(sketch, "E52", {"start": v(-2000, 6574.27) * mm, "end": v(-2000, 3294.27) * mm});
            skLineSegment(sketch, "E53", {"start": v(-2000, 3294.27) * mm, "end": v(-4000, 3294.27) * mm});
            skLineSegment(sketch, "E54", {"start": v(-4000, 3294.27) * mm, "end": v(-4000, 0) * mm});
            skLineSegment(sketch, "E55", {"start": v(-4000, 0) * mm, "end": v(0, 0) * mm});
            skLineSegment(sketch, "E56", {"start": v(0, 0) * mm, "end": v(0, 9854.27) * mm});
            skLineSegment(sketch, "E57.0", {"start": v(-200, 200) * mm, "end": v(-200, 9654.27) * mm});
            skLineSegment(sketch, "E57.1", {"start": v(-3800, 200) * mm, "end": v(-200, 200) * mm});
            skLineSegment(sketch, "E57.2", {"start": v(-200, 9654.27) * mm, "end": v(-3800, 9654.27) * mm});
            skLineSegment(sketch, "E57.3", {"start": v(-3800, 3094.27) * mm, "end": v(-3800, 200) * mm});
            skLineSegment(sketch, "E57.4", {"start": v(-3800, 9654.27) * mm, "end": v(-3800, 6774.27) * mm});
            skLineSegment(sketch, "E57.5", {"start": v(-3800, 6774.27) * mm, "end": v(-1800, 6774.27) * mm});
            skLineSegment(sketch, "E57.6", {"start": v(-1800, 6774.27) * mm, "end": v(-1800, 3094.27) * mm});
            skLineSegment(sketch, "E57.7", {"start": v(-1800, 3094.27) * mm, "end": v(-3800, 3094.27) * mm});
            skSolve(sketch);
        }
        {
            var Q0;
            Q0=makeQuery(id+"F37.imprint","IMPRINT",FACE,{"disambiguationData":[TD([[makeQuery(id+"F37.imprint","IMPRINT",EDGE,{"derivedFrom":sQuery(id+"F37.wireOp",EDGE,"E50")}),1.0]])]});
            extrude(context, id + "F38", {"entities" : qUnion([Q0]), "depth" : 2400 * mm, "offsetDistance" : 25 * mm});
        }
        {
            var Q0;
            Q0=makeQuery(id+"F38.opExtrude","SWEPT_FACE",FACE,{"disambiguationData":[OSD([sQuery(id+"F37.wireOp",EDGE,"E56")])]});
            var sketch = newSketch(context, id + "F39", { "sketchPlane" : qUnion([Q0])});
            skLineSegment(sketch, "E58.bottom", {"start": v(3838.63, 0) * mm, "end": v(4738.63, 0) * mm});
            skLineSegment(sketch, "E58.top", {"start": v(3838.63, 2000) * mm, "end": v(4738.63, 2000) * mm});
            skLineSegment(sketch, "E58.left", {"start": v(3838.63, 0) * mm, "end": v(3838.63, 2000) * mm});
            skLineSegment(sketch, "E58.right", {"start": v(4738.63, 0) * mm, "end": v(4738.63, 2000) * mm});
            skSolve(sketch);
        }
        {
            var Q0;
            Q0 = qSketchRegion(id + "F39", true);
            extrude(context, id + "F40", {"entities" : qUnion([Q0]), "operationType" : NewBodyOperationType.REMOVE, "oppositeDirection" : true, "depth" : 200 * mm, "offsetDistance" : 25 * mm});
        }
        {
            var Q0;
            Q0=makeQuery(id+"F36.opExtrude","CAP_FACE",FACE,{"disambiguationData":[OSD([sQuery(id+"F35.wireOp",EDGE,"E42"),sQuery(id+"F35.wireOp",EDGE,"E43"),sQuery(id+"F35.wireOp",EDGE,"E44"),sQuery(id+"F35.wireOp",EDGE,"E45"),sQuery(id+"F35.wireOp",EDGE,"E46"),sQuery(id+"F35.wireOp",EDGE,"E47"),sQuery(id+"F35.wireOp",EDGE,"E48"),sQuery(id+"F35.wireOp",EDGE,"E49")])],"isStart":true});
            var sketch = newSketch(context, id + "F41", { "sketchPlane" : qUnion([Q0])});
            skLineSegment(sketch, "E59", {"start": v(-198.73, 4927.14) * mm, "end": v(-1798.73, 4927.14) * mm});
            skPoint(sketch, "E59.startSnap0", {"position": v(0, 4927.14) * mm});
            skPoint(sketch, "E59.endSnap0", {"position": v(0, 4927.14) * mm});
            skLineSegment(sketch, "E60.0", {"start": v(-198.73, 5027.14) * mm, "end": v(-1798.73, 5027.14) * mm});
            skLineSegment(sketch, "E61", {"start": v(-1798.73, 4927.14) * mm, "end": v(-1798.73, 5027.14) * mm});
            skLineSegment(sketch, "E62", {"start": v(-198.73, 5027.14) * mm, "end": v(-198.73, 4927.14) * mm});
            skSolve(sketch);
        }
        {
            var Q0;
            Q0 = qSketchRegion(id + "F41", true);
            extrude(context, id + "F42", {"entities" : qUnion([Q0]), "depth" : 2400 * mm, "offsetDistance" : 25 * mm});
        }
        {
            var Q0;
            Q0=makeQuery(id+"F42.opExtrude","SWEPT_FACE",FACE,{"disambiguationData":[OSD([sQuery(id+"F41.wireOp",EDGE,"E59")])]});
            var sketch = newSketch(context, id + "F43", { "sketchPlane" : qUnion([Q0])});
            skLineSegment(sketch, "E63.bottom", {"start": v(-1387.2, 0) * mm, "end": v(-487.2, 0) * mm});
            skLineSegment(sketch, "E63.top", {"start": v(-1387.2, 2000) * mm, "end": v(-487.2, 2000) * mm});
            skLineSegment(sketch, "E63.left", {"start": v(-1387.2, 0) * mm, "end": v(-1387.2, 2000) * mm});
            skLineSegment(sketch, "E63.right", {"start": v(-487.2, 0) * mm, "end": v(-487.2, 2000) * mm});
            skSolve(sketch);
        }
        {
            var Q0;
            Q0 = qSketchRegion(id + "F43", true);
            extrude(context, id + "F44", {"entities" : qUnion([Q0]), "operationType" : NewBodyOperationType.REMOVE, "depth" : 1770 * mm, "offsetDistance" : 25 * mm});
        }
    });
